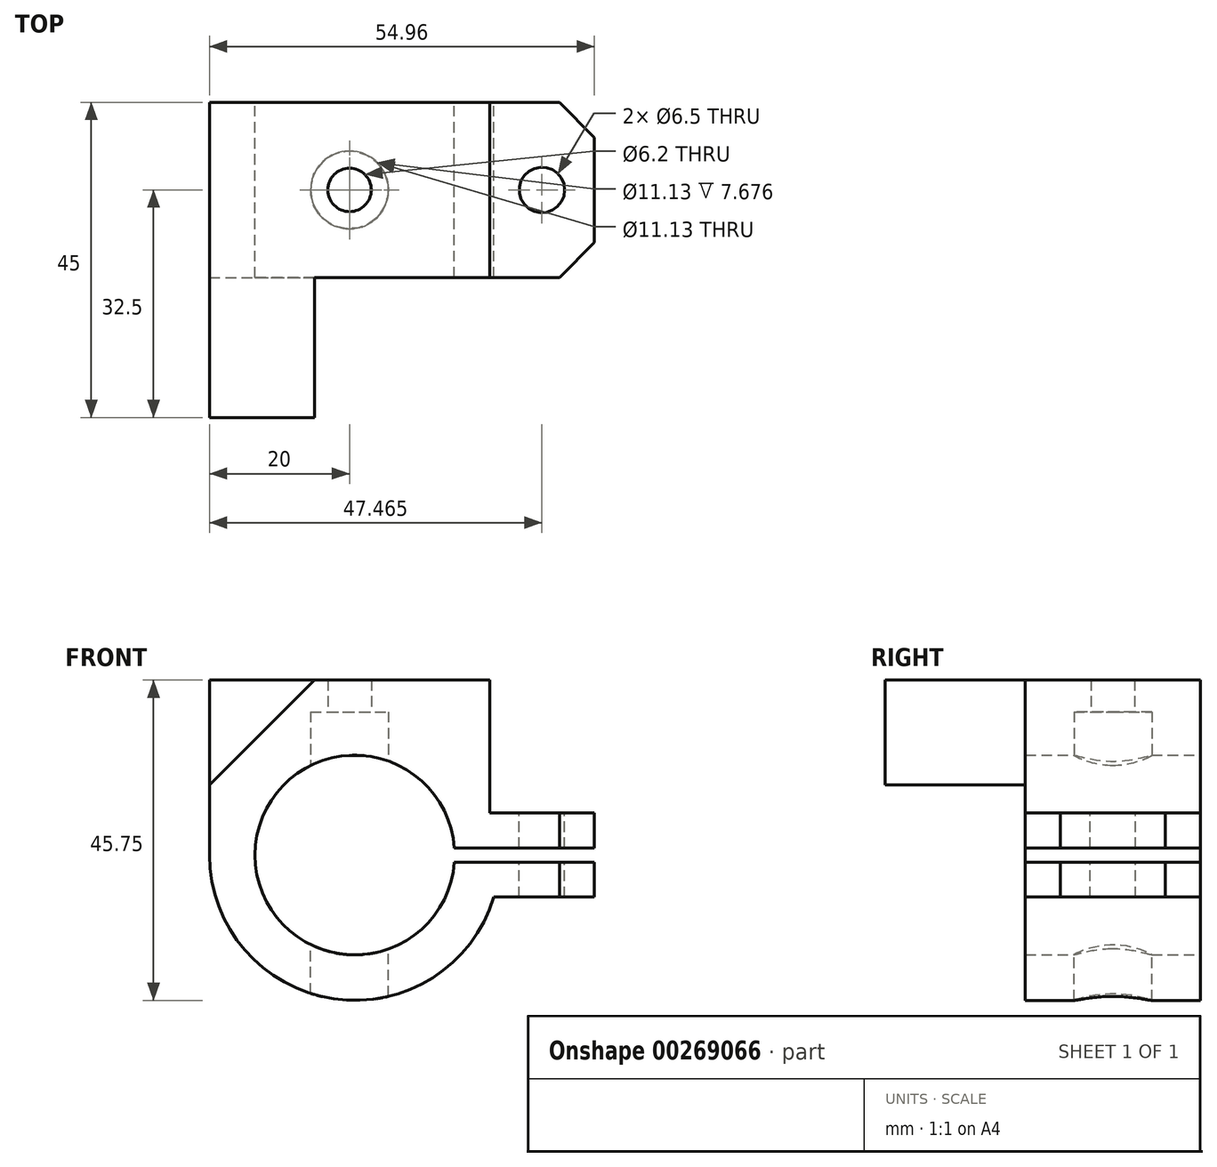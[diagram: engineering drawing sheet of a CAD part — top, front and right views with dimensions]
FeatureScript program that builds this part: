
annotation { "Feature Type Name" : "Feature", "Feature Type Description" : "" }
export const myFeature = defineFeature(function(context is Context, id is Id, definition is map)
    precondition{}
    {
        {
            var Q0;
            Q0=qCreatedBy(makeId("Front.planeOp"),FACE);
            var sketch = newSketch(context, id + "F0", { "sketchPlane" : qUnion([Q0])});
            skArc(sketch, "E0", {"start": v(14.21, 1) * mm, "mid": v(-14.25, 0) * mm, "end": v(14.21, -1) * mm});
            skLineSegment(sketch, "E1.0", {"start": v(14.21, 1) * mm, "end": v(34.21, 1) * mm});
            skLineSegment(sketch, "E2.0", {"start": v(14.21, -1) * mm, "end": v(34.21, -1) * mm});
            skLineSegment(sketch, "E3.0", {"start": v(19.25, 6) * mm, "end": v(34.21, 6) * mm});
            skLineSegment(sketch, "E4.0", {"start": v(19.86, -6) * mm, "end": v(34.21, -6) * mm});
            skLineSegment(sketch, "E5", {"start": v(34.21, 6) * mm, "end": v(34.21, 1) * mm});
            skLineSegment(sketch, "E6", {"start": v(34.21, -1) * mm, "end": v(34.21, -6) * mm});
            skLineSegment(sketch, "E7", {"start": v(19.25, 25) * mm, "end": v(19.25, 6) * mm});
            skLineSegment(sketch, "E8", {"start": v(-20.75, 25) * mm, "end": v(-20.75, 0) * mm});
            skArc(sketch, "E9", {"start": v(-20.75, 0) * mm, "mid": v(-3.03, -20.53) * mm, "end": v(19.86, -6) * mm});
            skLineSegment(sketch, "E10", {"start": v(-20.75, 25) * mm, "end": v(19.25, 25) * mm});
            skSolve(sketch);
        }
        {
            var Q0;
            Q0 = qSketchRegion(id + "F0", true);
            extrude(context, id + "F1", {"entities" : qUnion([Q0]), "depth" : 25 * mm});
        }
        {
            var Q0;
            Q0=makeQuery(id+"F1.opExtrude","SWEPT_FACE",FACE,{"disambiguationData":[OSD([sQuery(id+"F0.wireOp",EDGE,"E10")])]});
            var sketch = newSketch(context, id + "F2", { "sketchPlane" : qUnion([Q0])});
            skLineSegment(sketch, "E11.0.0", {"start": v(19.25, 0) * mm, "end": v(-20.75, 0) * mm});
            skLineSegment(sketch, "E11.0.1", {"start": v(-20.75, 0) * mm, "end": v(-20.75, -25) * mm});
            skLineSegment(sketch, "E11.0.2", {"start": v(-20.75, -25) * mm, "end": v(19.25, -25) * mm});
            skLineSegment(sketch, "E11.0.3", {"start": v(19.25, -25) * mm, "end": v(19.25, 0) * mm});
            skPoint(sketch, "E12", {"position": v(-0.75, -12.5) * mm});
            skSolve(sketch);
        }
        {
            var Q0;
            Q0=qCreatedBy(makeId("Top.planeOp"),FACE);
            var sketch = newSketch(context, id + "F3", { "sketchPlane" : qUnion([Q0])});
            skCircle(sketch, "E13.0", {"center": v(-0.75, -12.5) * mm, "radius": 2.5 * mm});
            skSolve(sketch);
        }
        {
            var Q0;
            Q0=sQuery(id+"F3.wireOp",VERTEX,"E13.0.center");
            var Q1;
            Q1=makeQuery(id+"F1.opExtrude","SWEPT_BODY",BODY,{"disambiguationData":[OSD([sQuery(id+"F0.wireOp",EDGE,"E0"),sQuery(id+"F0.wireOp",EDGE,"E1.0"),sQuery(id+"F0.wireOp",EDGE,"E2.0"),sQuery(id+"F0.wireOp",EDGE,"E3.0"),sQuery(id+"F0.wireOp",EDGE,"E4.0"),sQuery(id+"F0.wireOp",EDGE,"E5"),sQuery(id+"F0.wireOp",EDGE,"E6"),sQuery(id+"F0.wireOp",EDGE,"E7"),sQuery(id+"F0.wireOp",EDGE,"E8"),sQuery(id+"F0.wireOp",EDGE,"E9"),sQuery(id+"F0.wireOp",EDGE,"E10")])]});
            hole(context, id + "F4", {"style" : HoleStyle.C_BORE, "endStyle" : HoleEndStyle.BLIND, "oppositeDirection" : true, "holeDiameter" : 6.2 * mm, "cBoreDiameter" : 11.13 * mm, "cBoreDepth" : 6.2 * mm, "holeDepth" : 15 * mm, "tappedDepth" : 12 * mm, "tapClearance" : 3, "locations" : qUnion([Q0]), "scope" : qUnion([Q1])});
        }
        {
            var Q0;
            Q0=makeQuery(id+"F1.opExtrude","SWEPT_FACE",FACE,{"disambiguationData":[OSD([sQuery(id+"F0.wireOp",EDGE,"E3.0")])]});
            var sketch = newSketch(context, id + "F5", { "sketchPlane" : qUnion([Q0])});
            skPoint(sketch, "E14", {"position": v(26.71, -12.5) * mm});
            skSolve(sketch);
        }
        {
            var Q0;
            Q0=sQuery(id+"F5.wireOp",VERTEX,"E14");
            var Q1;
            Q1=makeQuery(id+"F1.opExtrude","SWEPT_BODY",BODY,{"disambiguationData":[OSD([sQuery(id+"F0.wireOp",EDGE,"E0"),sQuery(id+"F0.wireOp",EDGE,"E1.0"),sQuery(id+"F0.wireOp",EDGE,"E2.0"),sQuery(id+"F0.wireOp",EDGE,"E3.0"),sQuery(id+"F0.wireOp",EDGE,"E4.0"),sQuery(id+"F0.wireOp",EDGE,"E5"),sQuery(id+"F0.wireOp",EDGE,"E6"),sQuery(id+"F0.wireOp",EDGE,"E7"),sQuery(id+"F0.wireOp",EDGE,"E8"),sQuery(id+"F0.wireOp",EDGE,"E9"),sQuery(id+"F0.wireOp",EDGE,"E10")])]});
            hole(context, id + "F6", {"style" : HoleStyle.SIMPLE, "endStyle" : HoleEndStyle.BLIND, "holeDiameter" : 6.5 * mm, "holeDepth" : 15 * mm, "tappedDepth" : 12 * mm, "tapClearance" : 3, "locations" : qUnion([Q0]), "scope" : qUnion([Q1])});
        }
        {
            var Q0;
            Q0=sQuery(id+"F3.wireOp",VERTEX,"E13.0.center");
            var Q1;
            Q1=makeQuery(id+"F1.opExtrude","SWEPT_BODY",BODY,{"disambiguationData":[OSD([sQuery(id+"F0.wireOp",EDGE,"E0"),sQuery(id+"F0.wireOp",EDGE,"E1.0"),sQuery(id+"F0.wireOp",EDGE,"E2.0"),sQuery(id+"F0.wireOp",EDGE,"E3.0"),sQuery(id+"F0.wireOp",EDGE,"E4.0"),sQuery(id+"F0.wireOp",EDGE,"E5"),sQuery(id+"F0.wireOp",EDGE,"E6"),sQuery(id+"F0.wireOp",EDGE,"E7"),sQuery(id+"F0.wireOp",EDGE,"E8"),sQuery(id+"F0.wireOp",EDGE,"E9"),sQuery(id+"F0.wireOp",EDGE,"E10")])]});
            hole(context, id + "F7", {"style" : HoleStyle.SIMPLE, "endStyle" : HoleEndStyle.BLIND, "holeDiameter" : 11.13 * mm, "holeDepth" : 15 * mm, "tappedDepth" : 12 * mm, "tapClearance" : 3, "locations" : qUnion([Q0]), "scope" : qUnion([Q1])});
        }
        {
            var Q0;
            Q0=makeQuery(id+"F1.opExtrude","CAP_EDGE",EDGE,{"disambiguationData":[OSD([sQuery(id+"F0.wireOp",EDGE,"E5")])],"isStart":false});
            var Q1;
            Q1=makeQuery(id+"F1.opExtrude","CAP_EDGE",EDGE,{"disambiguationData":[OSD([sQuery(id+"F0.wireOp",EDGE,"E6")])],"isStart":false});
            var Q2;
            Q2=makeQuery(id+"F1.opExtrude","CAP_EDGE",EDGE,{"disambiguationData":[OSD([sQuery(id+"F0.wireOp",EDGE,"E6")])],"isStart":true});
            var Q3;
            Q3=makeQuery(id+"F1.opExtrude","CAP_EDGE",EDGE,{"disambiguationData":[OSD([sQuery(id+"F0.wireOp",EDGE,"E5")])],"isStart":true});
            chamfer(context, id + "F8", {"entities" : qUnion([Q0, Q1, Q2, Q3]), "width" : 5 * mm, "tangentPropagation" : true});
        }
        {
            var Q0;
            Q0=makeQuery(id+"F1.opExtrude","CAP_FACE",FACE,{"disambiguationData":[OSD([sQuery(id+"F0.wireOp",EDGE,"E0"),sQuery(id+"F0.wireOp",EDGE,"E1.0"),sQuery(id+"F0.wireOp",EDGE,"E2.0"),sQuery(id+"F0.wireOp",EDGE,"E3.0"),sQuery(id+"F0.wireOp",EDGE,"E4.0"),sQuery(id+"F0.wireOp",EDGE,"E5"),sQuery(id+"F0.wireOp",EDGE,"E6"),sQuery(id+"F0.wireOp",EDGE,"E7"),sQuery(id+"F0.wireOp",EDGE,"E8"),sQuery(id+"F0.wireOp",EDGE,"E9"),sQuery(id+"F0.wireOp",EDGE,"E10")])],"isStart":false});
            var sketch = newSketch(context, id + "F9", { "sketchPlane" : qUnion([Q0])});
            skLineSegment(sketch, "E15", {"start": v(-20.75, 25) * mm, "end": v(-20.75, 10) * mm});
            skLineSegment(sketch, "E16", {"start": v(-20.75, 10) * mm, "end": v(-5.75, 25) * mm});
            skLineSegment(sketch, "E17", {"start": v(-5.75, 25) * mm, "end": v(-20.75, 25) * mm});
            skSolve(sketch);
        }
        {
            var Q0;
            Q0=makeQuery(id+"F9.imprint","IMPRINT",FACE,{"disambiguationData":[TD([[makeQuery(id+"F9.imprint","IMPRINT",EDGE,{"derivedFrom":sQuery(id+"F9.wireOp",EDGE,"E15")}),1.0]])]});
            extrude(context, id + "F10", {"entities" : qUnion([Q0]), "operationType" : NewBodyOperationType.ADD, "depth" : 20 * mm});
        }
        {
            var Q0;
            Q0=makeQuery(id+"F10.opExtrude","SWEPT_FACE",FACE,{"disambiguationData":[OSD([sQuery(id+"F9.wireOp",EDGE,"E16")])]});
            var sketch = newSketch(context, id + "F11", { "sketchPlane" : qUnion([Q0])});
            skLineSegment(sketch, "E18", {"start": v(13.61, 45) * mm, "end": v(-7.6, 25) * mm});
            skLineSegment(sketch, "E19", {"start": v(-7.6, 25) * mm, "end": v(-7.6, 45) * mm});
            skLineSegment(sketch, "E20", {"start": v(-7.6, 45) * mm, "end": v(13.61, 25) * mm});
            skCircle(sketch, "E21", {"center": v(3, 35) * mm, "radius": 7.65 * mm});
            skSolve(sketch);
        }
        {
            var Q0;
            {var subQ0=sQuery(id+"F11.wireOp",EDGE,"E21");var subQ1=sQuery(id+"F11.wireOp",EDGE,"E18");var subQ2=makeQuery(id+"F11.imprint","INTERSECT",VERTEX,{"disambiguationData":[OD(0.0)],"derivedFrom":[subQ1,subQ0]});Q0=makeQuery(id+"F11.imprint","IMPRINT",FACE,{"disambiguationData":[TD([[makeQuery(id+"F11.imprint","IMPRINT",EDGE,{"disambiguationData":[TD([[subQ2,-1.0]])],"derivedFrom":subQ1}),-1.0]])]});}
            var Q1;
            {var subQ0=sQuery(id+"F11.wireOp",EDGE,"E20");var subQ1=sQuery(id+"F11.wireOp",EDGE,"E18");var subQ2=makeQuery(id+"F11.imprint","INTERSECT",VERTEX,{"derivedFrom":[subQ1,subQ0]});Q1=makeQuery(id+"F11.imprint","IMPRINT",FACE,{"disambiguationData":[TD([[makeQuery(id+"F11.imprint","IMPRINT",EDGE,{"disambiguationData":[TD([[subQ2,-1.0]])],"derivedFrom":subQ1}),-1.0]])]});}
            var Q2;
            {var subQ0=sQuery(id+"F11.wireOp",EDGE,"E21");var subQ1=sQuery(id+"F11.wireOp",EDGE,"E18");var subQ2=makeQuery(id+"F11.imprint","INTERSECT",VERTEX,{"disambiguationData":[OD(0.0)],"derivedFrom":[subQ1,subQ0]});Q2=makeQuery(id+"F11.imprint","IMPRINT",FACE,{"disambiguationData":[TD([[makeQuery(id+"F11.imprint","IMPRINT",EDGE,{"disambiguationData":[TD([[subQ2,-1.0]])],"derivedFrom":subQ1}),1.0]])]});}
            var Q3;
            {var subQ0=sQuery(id+"F11.wireOp",EDGE,"E20");var subQ1=sQuery(id+"F11.wireOp",EDGE,"E18");var subQ2=makeQuery(id+"F11.imprint","INTERSECT",VERTEX,{"derivedFrom":[subQ1,subQ0]});Q3=makeQuery(id+"F11.imprint","IMPRINT",FACE,{"disambiguationData":[TD([[makeQuery(id+"F11.imprint","IMPRINT",EDGE,{"disambiguationData":[TD([[subQ2,-1.0]])],"derivedFrom":subQ1}),1.0]])]});}
            extrude(context, id + "F12", {"entities" : qUnion([Q0, Q1, Q2, Q3]), "operationType" : NewBodyOperationType.REMOVE, "oppositeDirection" : true, "depth" : 25 * mm});
        }
    });
